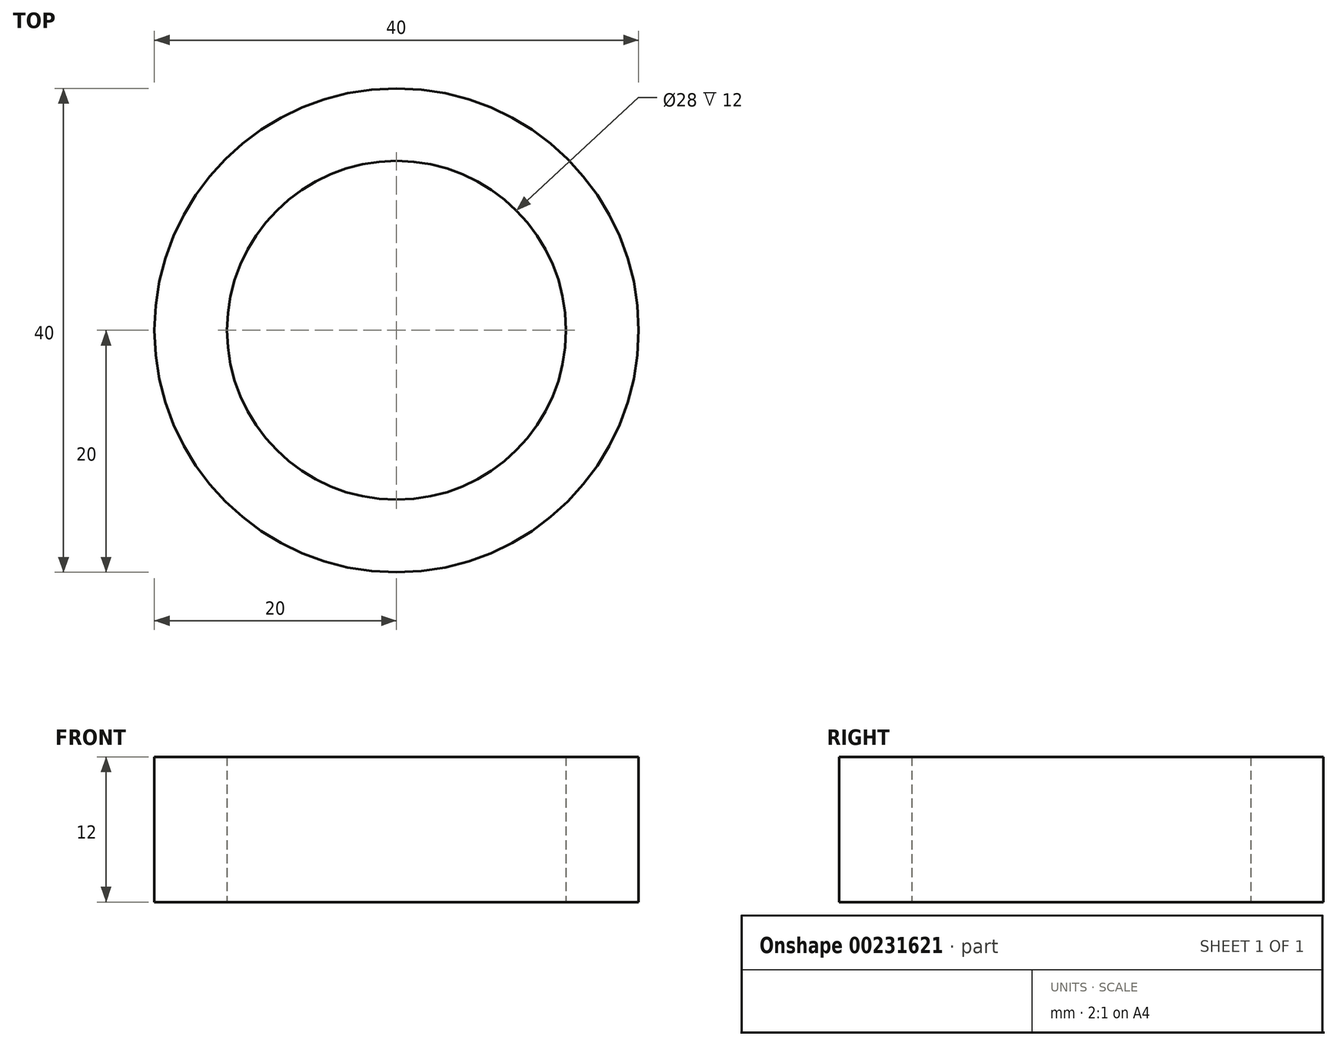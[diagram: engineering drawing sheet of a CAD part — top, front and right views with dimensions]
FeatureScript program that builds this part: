
annotation { "Feature Type Name" : "Feature", "Feature Type Description" : "" }
export const myFeature = defineFeature(function(context is Context, id is Id, definition is map)
    precondition{}
    {
        {
            var Q0;
            Q0=qCreatedBy(makeId("Top.planeOp"),FACE);
            var sketch = newSketch(context, id + "F0", { "sketchPlane" : qUnion([Q0])});
            skCircle(sketch, "E0", {"center": v(0, 0) * mm, "radius": 14 * mm});
            skCircle(sketch, "E1", {"center": v(0, 0) * mm, "radius": 20 * mm});
            skSolve(sketch);
        }
        {
            var Q0;
            Q0 = qSketchRegion(id + "F0", true);
            extrude(context, id + "F1", {"entities" : qUnion([Q0]), "depth" : 12 * mm});
        }
    });
